# Revit family: Door_Vault
name_source: partatom
category: Doors
units: mm (PartAtom-declared; Revit-internal decimal feet)

## family parameters
Always vertical = Yes
Classification Number = 23.40.70.27.17
Cut with Voids When Loaded = No
Host = Wall
Room Calculation Point = No
Shared = No

## types (1)
- 36x78
    Assembly Code = E1010120
    Construction Details = http://www.arcat.com
    Description = 36x78 Vault Door
    Door Material = ARCAT - Metal - Steel - BHMA645 - Bright Nickel Plated
    Expected Lifespan (Years) = 25
    Fire Rating = 2 Hour
    Frame Material = ARCAT - Metal - Stainless Steel - BHMA629 - Polished
    Frame Projection Ext. = 0' - 1 1/2"
    Frame Projection Int. = 0' - 1"
    Frame Width = 0' - 5"
    Function = Interior
    Height = 6' - 6"
    Hinge Type = Roller Thrust Bearing
    Keynote = 11020
    Lock Finish = ARCAT - Metal - Steel - BHMA632 - Bright Brass
    Lock Type = 3 Tumbler Group II Key Change Combination Lock
    Locking Mechanism = Live Bolting  (10)
    Maintenance Schedule (Months) = 3
    Manufacturer = Generic
    Manufacturer Fax = (203) 929-2444
    Manufacturer Website = http://www.arcat.com
    Model = Generic
    Product Data = http://www.arcat.com
    Product Properties = http://www.arcat.com
    Rough Height = 6' - 7 1/2"
    Rough Width = 3' - 3"
    Specification = http://www.arcat.com
    Thickness = 0' - 11"
    UL Rating = {Class M}{Class 1}{Class 2}{Class 3}
    Wall Closure = By host
    Warranty Duration (Years) = 5
    Width = 3' - 0"

## geometry (parser evidence)
native form markers: Sweep x5
no freeform markers — native parametric forms only
